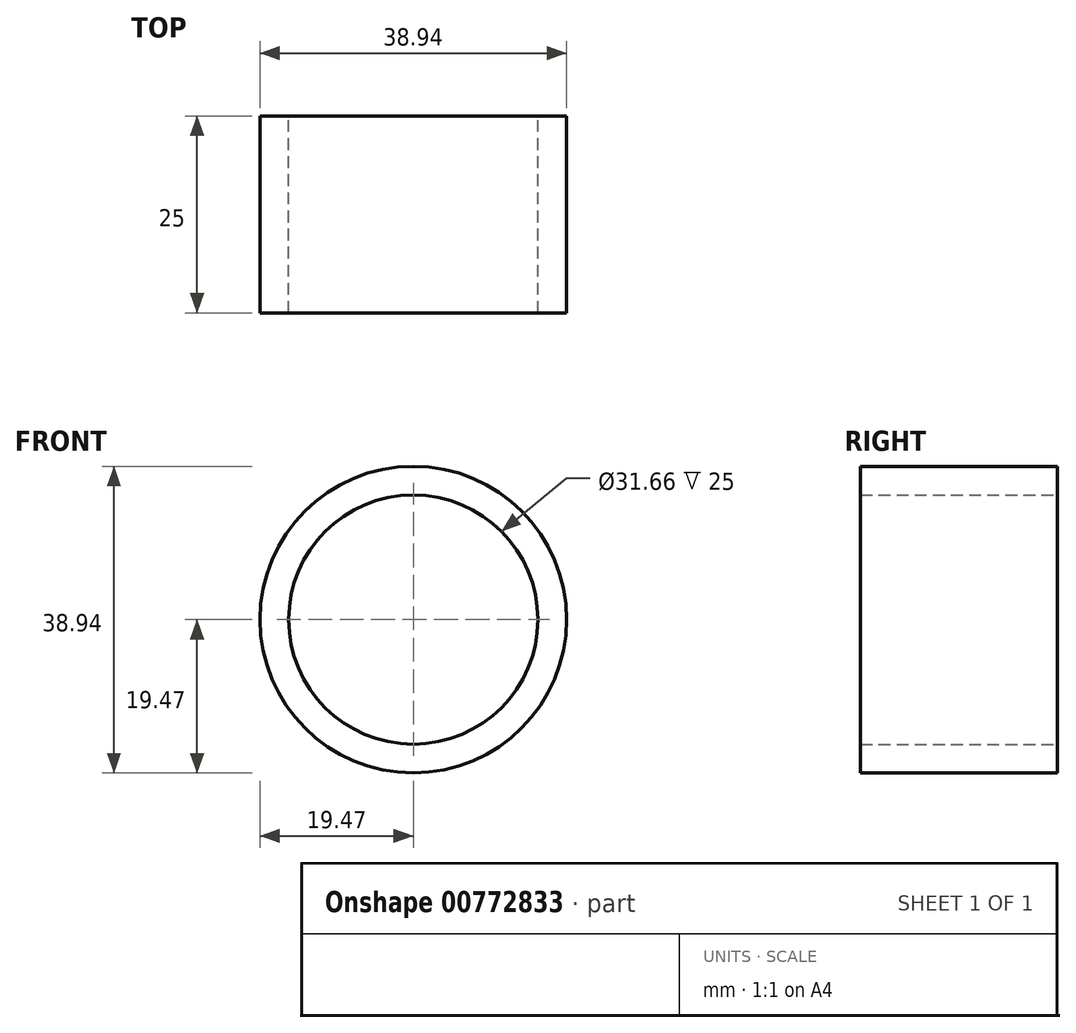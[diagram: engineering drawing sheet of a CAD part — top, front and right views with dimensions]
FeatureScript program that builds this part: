
annotation { "Feature Type Name" : "Feature", "Feature Type Description" : "" }
export const myFeature = defineFeature(function(context is Context, id is Id, definition is map)
    precondition{}
    {
        {
            var Q0;
            Q0=qCreatedBy(makeId("Front.planeOp"),FACE);
            var sketch = newSketch(context, id + "F0", { "sketchPlane" : qUnion([Q0])});
            skCircle(sketch, "E0", {"center": v(0, 0) * mm, "radius": 19.47 * mm});
            skCircle(sketch, "E1", {"center": v(0, 0) * mm, "radius": 15.83 * mm});
            skSolve(sketch);
        }
        {
            var Q0;
            Q0 = qSketchRegion(id + "F0", true);
            extrude(context, id + "F1", {"entities" : qUnion([Q0]), "depth" : 25 * mm, "offsetDistance" : 25 * mm});
        }
    });
